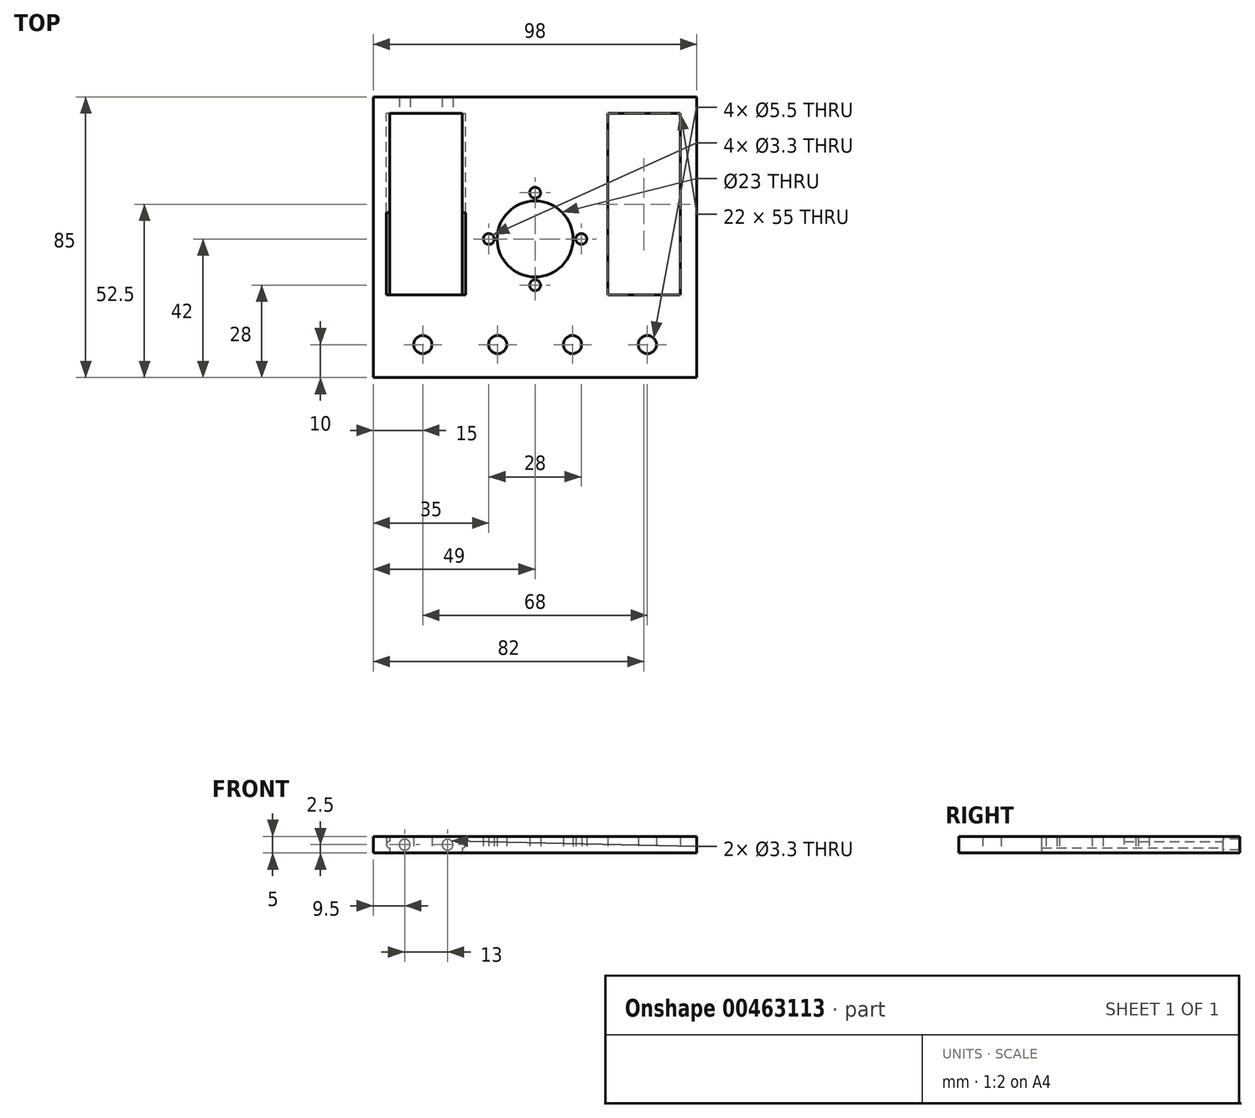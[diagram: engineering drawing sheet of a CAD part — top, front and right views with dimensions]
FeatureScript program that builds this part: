
annotation { "Feature Type Name" : "Feature", "Feature Type Description" : "" }
export const myFeature = defineFeature(function(context is Context, id is Id, definition is map)
    precondition{}
    {
        {
            var Q0;
            Q0=qCreatedBy(makeId("Top.planeOp"),FACE);
            var sketch = newSketch(context, id + "F0", { "sketchPlane" : qUnion([Q0])});
            skCircle(sketch, "E0", {"center": v(0, 0) * mm, "radius": 11.5 * mm});
            skLineSegment(sketch, "E1.bottom", {"start": v(-49, -42) * mm, "end": v(49, -42) * mm});
            skLineSegment(sketch, "E1.top", {"start": v(-49, 43) * mm, "end": v(49, 43) * mm});
            skLineSegment(sketch, "E1.left", {"start": v(-49, -42) * mm, "end": v(-49, 43) * mm});
            skLineSegment(sketch, "E1.right", {"start": v(49, -42) * mm, "end": v(49, 43) * mm});
            skLineSegment(sketch, "E2.bottom", {"start": v(-44, -17) * mm, "end": v(-22, -17) * mm});
            skLineSegment(sketch, "E2.top", {"start": v(-44, 38) * mm, "end": v(-22, 38) * mm});
            skLineSegment(sketch, "E2.left", {"start": v(-44, -17) * mm, "end": v(-44, 38) * mm});
            skLineSegment(sketch, "E2.right", {"start": v(-22, -17) * mm, "end": v(-22, 38) * mm});
            skLineSegment(sketch, "E3.MirrorCS", {"start": v(44, -17) * mm, "end": v(44, 38) * mm});
            skLineSegment(sketch, "E4.MirrorCS", {"start": v(44, -17) * mm, "end": v(22, -17) * mm});
            skLineSegment(sketch, "E5.MirrorCS", {"start": v(22, -17) * mm, "end": v(22, 38) * mm});
            skLineSegment(sketch, "E6.MirrorCS", {"start": v(44, 38) * mm, "end": v(22, 38) * mm});
            skPoint(sketch, "E7.positionSnap0", {"position": v(0, -42) * mm});
            skPoint(sketch, "E8", {"position": v(-34, -32) * mm});
            skPoint(sketch, "E9.1.0.0", {"position": v(-11.33, -32) * mm});
            skPoint(sketch, "E9.2.0.0", {"position": v(11.33, -32) * mm});
            skLineSegment(sketch, "E9.direction1", {"start": v(-34, -32) * mm, "end": v(-11.33, -32) * mm, "construction": true});
            skPoint(sketch, "E10.0.3.0", {"position": v(34, -32) * mm});
            skPoint(sketch, "E11", {"position": v(-14, 0) * mm});
            skPoint(sketch, "E12.1.0", {"position": v(0, -14) * mm});
            skPoint(sketch, "E12.2.0", {"position": v(14, 0) * mm});
            skPoint(sketch, "E13.0.3.0", {"position": v(0, 14) * mm});
            skSolve(sketch);
        }
        {
            var Q0;
            Q0=makeQuery(id+"F0.imprint","IMPRINT",FACE,{"disambiguationData":[TD([[makeQuery(id+"F0.imprint","IMPRINT",EDGE,{"derivedFrom":sQuery(id+"F0.wireOp",EDGE,"E0")}),-1.0]])]});
            extrude(context, id + "F1", {"entities" : qUnion([Q0]), "depth" : 5 * mm});
        }
        {
            var Q0;
            Q0=makeQuery(id+"F1.opExtrude","SWEPT_FACE",FACE,{"disambiguationData":[OSD([sQuery(id+"F0.wireOp",EDGE,"E2.top")])]});
            var sketch = newSketch(context, id + "F2", { "sketchPlane" : qUnion([Q0])});
            skPoint(sketch, "E14", {"position": v(-44, 1.5) * mm});
            skPoint(sketch, "E15.0.1.0", {"position": v(-44, 2.5) * mm});
            skPoint(sketch, "E15.0.2.0", {"position": v(-44, 3.5) * mm});
            skPoint(sketch, "E15.1.0.0", {"position": v(-33, 1.5) * mm});
            skPoint(sketch, "E15.1.1.0", {"position": v(-33, 2.5) * mm});
            skPoint(sketch, "E15.1.2.0", {"position": v(-33, 3.5) * mm});
            skPoint(sketch, "E15.2.0.0", {"position": v(-22, 1.5) * mm});
            skPoint(sketch, "E15.2.1.0", {"position": v(-22, 2.5) * mm});
            skPoint(sketch, "E15.2.2.0", {"position": v(-22, 3.5) * mm});
            skLineSegment(sketch, "E15.direction1", {"start": v(-44, 1.5) * mm, "end": v(-33, 1.5) * mm, "construction": true});
            skLineSegment(sketch, "E15.direction2", {"start": v(-44, 1.5) * mm, "end": v(-44, 2.5) * mm, "construction": true});
            skArc(sketch, "E16", {"start": v(-44, 3.5) * mm, "mid": v(-45, 2.5) * mm, "end": v(-44, 1.5) * mm});
            skLineSegment(sketch, "E17", {"start": v(-44, 3.5) * mm, "end": v(-44, 1.5) * mm});
            skLineSegment(sketch, "E18", {"start": v(-33, 3.5) * mm, "end": v(-33, 1.5) * mm, "construction": true});
            skArc(sketch, "E19.MirrorCS", {"start": v(-22, 3.5) * mm, "mid": v(-21, 2.5) * mm, "end": v(-22, 1.5) * mm});
            skLineSegment(sketch, "E20.MirrorCS", {"start": v(-22, 3.5) * mm, "end": v(-22, 1.5) * mm});
            skLineSegment(sketch, "E21.MirrorCS", {"start": v(-22, 1.5) * mm, "end": v(-33, 1.5) * mm, "construction": true});
            skLineSegment(sketch, "E22.MirrorCS", {"start": v(-22, 1.5) * mm, "end": v(-22, 2.5) * mm, "construction": true});
            skPoint(sketch, "E23", {"position": v(-39.5, 2.5) * mm});
            skPoint(sketch, "E24.MirrorP", {"position": v(-26.5, 2.5) * mm});
            skSolve(sketch);
        }
        {
            var Q0;
            Q0 = qSketchRegion(id + "F2", true);
            var Q1;
            Q1=makeQuery(id+"F1.opExtrude","SWEPT_FACE",FACE,{"disambiguationData":[OSD([sQuery(id+"F0.wireOp",EDGE,"E2.bottom")])]});
            var Q2;
            Q2=qCreatedBy(makeId("Origin.pointOp"),VERTEX);
            extrude(context, id + "F3", {"entities" : qUnion([Q0]), "operationType" : NewBodyOperationType.REMOVE, "endBound" : BoundingType.UP_TO_SURFACE, "endBoundEntityFace" : qUnion([Q1]), "endBoundEntityVertex" : qUnion([Q2]), "depth" : 25 * mm});
        }
        {
            var Q0;
            {var subQ0=sQuery(id+"F0.wireOp",EDGE,"E2.bottom");Q0=makeQuery(id+"F3.boolean.opBoolean","MERGE",FACE,{"derivedFrom":[makeQuery(id+"F1.opExtrude","SWEPT_FACE",FACE,{"disambiguationData":[OSD([subQ0])]}),makeQuery(id+"F3.opExtrude","CAP_FACE",FACE,{"disambiguationData":[OSD([subQ0]),ownerDisambiguation([makeQuery(id+"F2.imprint","IMPRINT",EDGE,{"derivedFrom":sQuery(id+"F2.wireOp",EDGE,"E16")})])],"isStart":false}),makeQuery(id+"F3.opExtrude","CAP_FACE",FACE,{"disambiguationData":[OSD([subQ0]),ownerDisambiguation([makeQuery(id+"F2.imprint","IMPRINT",EDGE,{"derivedFrom":sQuery(id+"F2.wireOp",EDGE,"E19.MirrorCS")})])],"isStart":false})]});}
            var sketch = newSketch(context, id + "F4", { "sketchPlane" : qUnion([Q0])});
            skPoint(sketch, "E25.oppositeSnap0", {"position": v(45, 2.5) * mm});
            skLineSegment(sketch, "E25.bottom", {"start": v(45, 5) * mm, "end": v(44, 5) * mm});
            skLineSegment(sketch, "E25.top", {"start": v(45, 2.5) * mm, "end": v(44, 2.5) * mm});
            skLineSegment(sketch, "E25.left", {"start": v(44, 5) * mm, "end": v(44, 2.5) * mm});
            skLineSegment(sketch, "E25.right", {"start": v(45, 5) * mm, "end": v(45, 2.5) * mm});
            skLineSegment(sketch, "E26", {"start": v(33, 5) * mm, "end": v(33, 0) * mm, "construction": true});
            skLineSegment(sketch, "E27.MirrorCS", {"start": v(22, 5) * mm, "end": v(22, 2.5) * mm});
            skLineSegment(sketch, "E28.MirrorCS", {"start": v(21, 5) * mm, "end": v(21, 2.5) * mm});
            skLineSegment(sketch, "E29.MirrorCS", {"start": v(21, 2.5) * mm, "end": v(22, 2.5) * mm});
            skPoint(sketch, "E30.MirrorP", {"position": v(21, 2.5) * mm});
            skLineSegment(sketch, "E31.MirrorCS", {"start": v(21, 5) * mm, "end": v(22, 5) * mm});
            skSolve(sketch);
        }
        {
            var Q0;
            Q0 = qSketchRegion(id + "F4", true);
            extrude(context, id + "F5", {"entities" : qUnion([Q0]), "operationType" : NewBodyOperationType.REMOVE, "depth" : 25 * mm});
        }
        {
            var Q0;
            Q0=sQuery(id+"F0.wireOp",VERTEX,"E8");
            var Q1;
            Q1=sQuery(id+"F0.wireOp",VERTEX,"E9.1.0.0");
            var Q2;
            Q2=sQuery(id+"F0.wireOp",VERTEX,"E9.2.0.0");
            var Q3;
            Q3=sQuery(id+"F0.wireOp",VERTEX,"E10.0.3.0");
            var Q4;
            Q4=makeQuery(id+"F1.opExtrude","SWEPT_BODY",BODY,{"disambiguationData":[OSD([sQuery(id+"F0.wireOp",EDGE,"E0"),sQuery(id+"F0.wireOp",EDGE,"E1.bottom"),sQuery(id+"F0.wireOp",EDGE,"E1.top"),sQuery(id+"F0.wireOp",EDGE,"E1.left"),sQuery(id+"F0.wireOp",EDGE,"E1.right"),sQuery(id+"F0.wireOp",EDGE,"E2.bottom"),sQuery(id+"F0.wireOp",EDGE,"E2.top"),sQuery(id+"F0.wireOp",EDGE,"E2.left"),sQuery(id+"F0.wireOp",EDGE,"E2.right"),sQuery(id+"F0.wireOp",EDGE,"E3.MirrorCS"),sQuery(id+"F0.wireOp",EDGE,"E4.MirrorCS"),sQuery(id+"F0.wireOp",EDGE,"E5.MirrorCS"),sQuery(id+"F0.wireOp",EDGE,"E6.MirrorCS")])]});
            hole(context, id + "F6", {"style" : HoleStyle.SIMPLE, "endStyle" : HoleEndStyle.THROUGH, "oppositeDirection" : true, "standardTappedOrClearance" : lookupTablePath({ "standard" : "ISO", "fit" : "Normal", "size" : "M5", "type" : "Clearance" }), "standardBlindInLast" : lookupTablePath({ "fit" : "Standard", "standard" : "ISO", "size" : "M5", "type" : "Clearance" }), "holeDiameter" : 5.5 * mm, "isTappedThrough" : true, "tappedDepth" : 12 * mm, "tapClearance" : 3, "locations" : qUnion([Q0, Q1, Q2, Q3]), "scope" : qUnion([Q4])});
        }
        {
            var Q0;
            Q0=sQuery(id+"F0.wireOp",VERTEX,"E11");
            var Q1;
            Q1=sQuery(id+"F0.wireOp",VERTEX,"E13.0.3.0");
            var Q2;
            Q2=sQuery(id+"F0.wireOp",VERTEX,"E12.2.0");
            var Q3;
            Q3=sQuery(id+"F0.wireOp",VERTEX,"E12.1.0");
            var Q4;
            Q4=makeQuery(id+"F1.opExtrude","SWEPT_BODY",BODY,{"disambiguationData":[OSD([sQuery(id+"F0.wireOp",EDGE,"E0"),sQuery(id+"F0.wireOp",EDGE,"E1.bottom"),sQuery(id+"F0.wireOp",EDGE,"E1.top"),sQuery(id+"F0.wireOp",EDGE,"E1.left"),sQuery(id+"F0.wireOp",EDGE,"E1.right"),sQuery(id+"F0.wireOp",EDGE,"E2.bottom"),sQuery(id+"F0.wireOp",EDGE,"E2.top"),sQuery(id+"F0.wireOp",EDGE,"E2.left"),sQuery(id+"F0.wireOp",EDGE,"E2.right"),sQuery(id+"F0.wireOp",EDGE,"E3.MirrorCS"),sQuery(id+"F0.wireOp",EDGE,"E4.MirrorCS"),sQuery(id+"F0.wireOp",EDGE,"E5.MirrorCS"),sQuery(id+"F0.wireOp",EDGE,"E6.MirrorCS")])]});
            hole(context, id + "F7", {"style" : HoleStyle.SIMPLE, "endStyle" : HoleEndStyle.THROUGH, "oppositeDirection" : true, "standardTappedOrClearance" : lookupTablePath({ "standard" : "ISO", "fit" : "Normal", "size" : "M3", "type" : "Clearance" }), "standardBlindInLast" : lookupTablePath({ "fit" : "Standard", "standard" : "ISO", "size" : "M3", "type" : "Clearance" }), "holeDiameter" : 3.3 * mm, "isTappedThrough" : true, "tappedDepth" : 12 * mm, "tapClearance" : 3, "locations" : qUnion([Q0, Q1, Q2, Q3]), "scope" : qUnion([Q4])});
        }
        {
            var Q0;
            Q0=sQuery(id+"F2.wireOp",VERTEX,"E24.MirrorP");
            var Q1;
            Q1=sQuery(id+"F2.wireOp",VERTEX,"E23");
            var Q2;
            Q2=makeQuery(id+"F1.opExtrude","SWEPT_BODY",BODY,{"disambiguationData":[OSD([sQuery(id+"F0.wireOp",EDGE,"E0"),sQuery(id+"F0.wireOp",EDGE,"E1.bottom"),sQuery(id+"F0.wireOp",EDGE,"E1.top"),sQuery(id+"F0.wireOp",EDGE,"E1.left"),sQuery(id+"F0.wireOp",EDGE,"E1.right"),sQuery(id+"F0.wireOp",EDGE,"E2.bottom"),sQuery(id+"F0.wireOp",EDGE,"E2.top"),sQuery(id+"F0.wireOp",EDGE,"E2.left"),sQuery(id+"F0.wireOp",EDGE,"E2.right"),sQuery(id+"F0.wireOp",EDGE,"E3.MirrorCS"),sQuery(id+"F0.wireOp",EDGE,"E4.MirrorCS"),sQuery(id+"F0.wireOp",EDGE,"E5.MirrorCS"),sQuery(id+"F0.wireOp",EDGE,"E6.MirrorCS")])]});
            hole(context, id + "F8", {"style" : HoleStyle.SIMPLE, "endStyle" : HoleEndStyle.THROUGH, "standardTappedOrClearance" : lookupTablePath({ "standard" : "ISO", "fit" : "Normal", "size" : "M3", "type" : "Clearance" }), "standardBlindInLast" : lookupTablePath({ "fit" : "Standard", "standard" : "ISO", "size" : "M3", "type" : "Clearance" }), "holeDiameter" : 3.3 * mm, "isTappedThrough" : true, "tappedDepth" : 12 * mm, "tapClearance" : 3, "locations" : qUnion([Q0, Q1]), "scope" : qUnion([Q2])});
        }
    });
